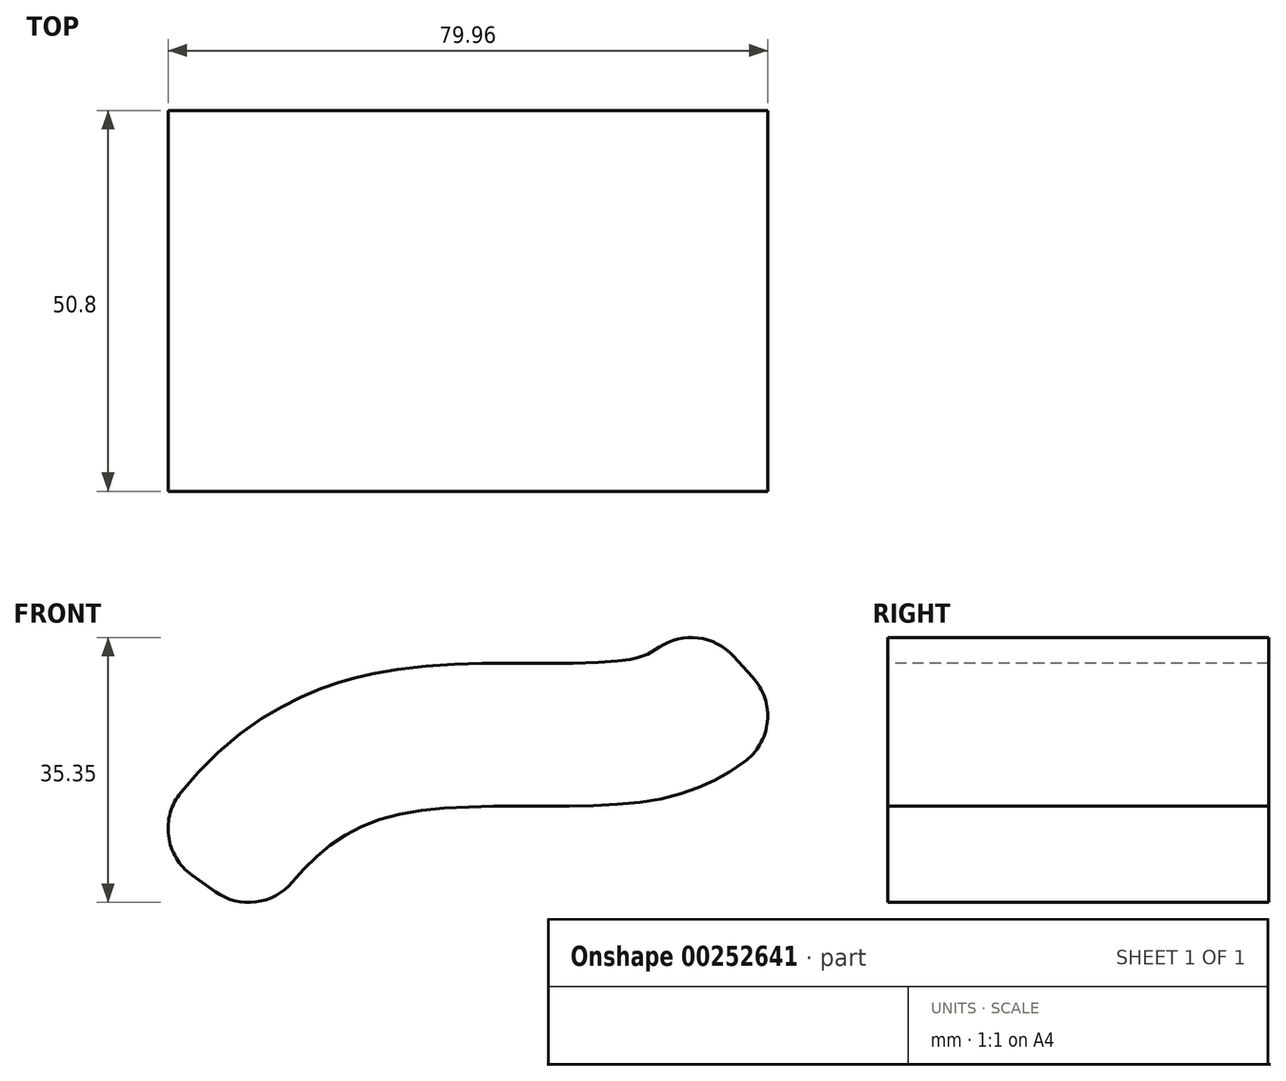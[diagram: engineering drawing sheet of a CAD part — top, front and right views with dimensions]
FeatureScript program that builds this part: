
annotation { "Feature Type Name" : "Feature", "Feature Type Description" : "" }
export const myFeature = defineFeature(function(context is Context, id is Id, definition is map)
    precondition{}
    {
        {
            var Q0;
            Q0=qCreatedBy(makeId("Front.planeOp"),FACE);
            var sketch = newSketch(context, id + "F0", { "sketchPlane" : qUnion([Q0])});
            skFitSpline(sketch, "E0", {"points": [v(-51.07, -3.13) * mm, v(-35.03, 10.88) * mm, v(2.58, 13.64) * mm, v(19.91, 23.97) * mm], "startDerivative": vector(41.22, 57.41) * mm, "endDerivative": vector(48.22, 44.13) * mm});
            skFitSpline(sketch, "E1.0", {"points": [v(-66.54, 7.98) * mm, v(-65.68, 9.17) * mm, v(-64.24, 11.2) * mm, v(-61.85, 14.23) * mm, v(-59.78, 16.64) * mm, v(-57.38, 19.13) * mm, v(-54.6, 21.62) * mm, v(-51.92, 23.61) * mm, v(-49.56, 25.1) * mm, v(-47.7, 26.16) * mm, v(-45.74, 27.14) * mm, v(-43.68, 28.02) * mm, v(-41.91, 28.68) * mm, v(-40.45, 29.14) * mm, v(-39.37, 29.46) * mm, v(-38.3, 29.74) * mm, v(-36.9, 30.08) * mm, v(-34.49, 30.58) * mm, v(-31.17, 31.06) * mm, v(-27.36, 31.4) * mm, v(-23.7, 31.58) * mm, v(-20.17, 31.66) * mm, v(-15.68, 31.68) * mm, v(-11.54, 31.66) * mm, v(-7.89, 31.7) * mm, v(-5.46, 31.8) * mm, v(-3.77, 31.93) * mm, v(-2.65, 32.06) * mm, v(-2.06, 32.15) * mm, v(-1.67, 32.22) * mm, v(-1.41, 32.27) * mm, v(-1.2, 32.32) * mm, v(-0.92, 32.38) * mm, v(-0.6, 32.47) * mm, v(-0.14, 32.62) * mm, v(0.37, 32.82) * mm, v(0.98, 33.12) * mm, v(1.65, 33.51) * mm, v(2.68, 34.21) * mm, v(4.3, 35.51) * mm, v(6.05, 37.1) * mm, v(7.05, 38.02) * mm]});
            skLineSegment(sketch, "E2", {"start": v(-66.54, 7.98) * mm, "end": v(-51.07, -3.13) * mm});
            skLineSegment(sketch, "E3", {"start": v(7.05, 38.02) * mm, "end": v(19.91, 23.97) * mm});
            skSolve(sketch);
        }
        {
            var Q0;
            Q0=makeQuery(id+"F0.imprint","IMPRINT",FACE,{"disambiguationData":[TD([[makeQuery(id+"F0.imprint","IMPRINT",EDGE,{"derivedFrom":sQuery(id+"F0.wireOp",EDGE,"E0")}),1.0]])]});
            extrude(context, id + "F1", {"entities" : qUnion([Q0]), "depth" : 50.8 * mm});
        }
        {
            var Q0;
            Q0=makeQuery(id+"F1.opExtrude","SWEPT_EDGE",EDGE,{"disambiguationData":[OSD([sQuery(id+"F0.wireOp",EDGE,"E1.0"),sQuery(id+"F0.wireOp",EDGE,"E3")])]});
            var Q1;
            Q1=makeQuery(id+"F1.opExtrude","SWEPT_EDGE",EDGE,{"disambiguationData":[OSD([sQuery(id+"F0.wireOp",EDGE,"E0"),sQuery(id+"F0.wireOp",EDGE,"E3")])]});
            var Q2;
            Q2=makeQuery(id+"F1.opExtrude","SWEPT_EDGE",EDGE,{"disambiguationData":[OSD([sQuery(id+"F0.wireOp",EDGE,"E1.0"),sQuery(id+"F0.wireOp",EDGE,"E2")])]});
            var Q3;
            Q3=makeQuery(id+"F1.opExtrude","SWEPT_EDGE",EDGE,{"disambiguationData":[OSD([sQuery(id+"F0.wireOp",EDGE,"E0"),sQuery(id+"F0.wireOp",EDGE,"E2")])]});
            fillet(context, id + "F2", {"entities" : qUnion([Q0, Q1, Q2, Q3]), "radius" : 7.62 * mm, "tangentPropagation" : true, "allowEdgeOverflow" : false});
        }
    });
